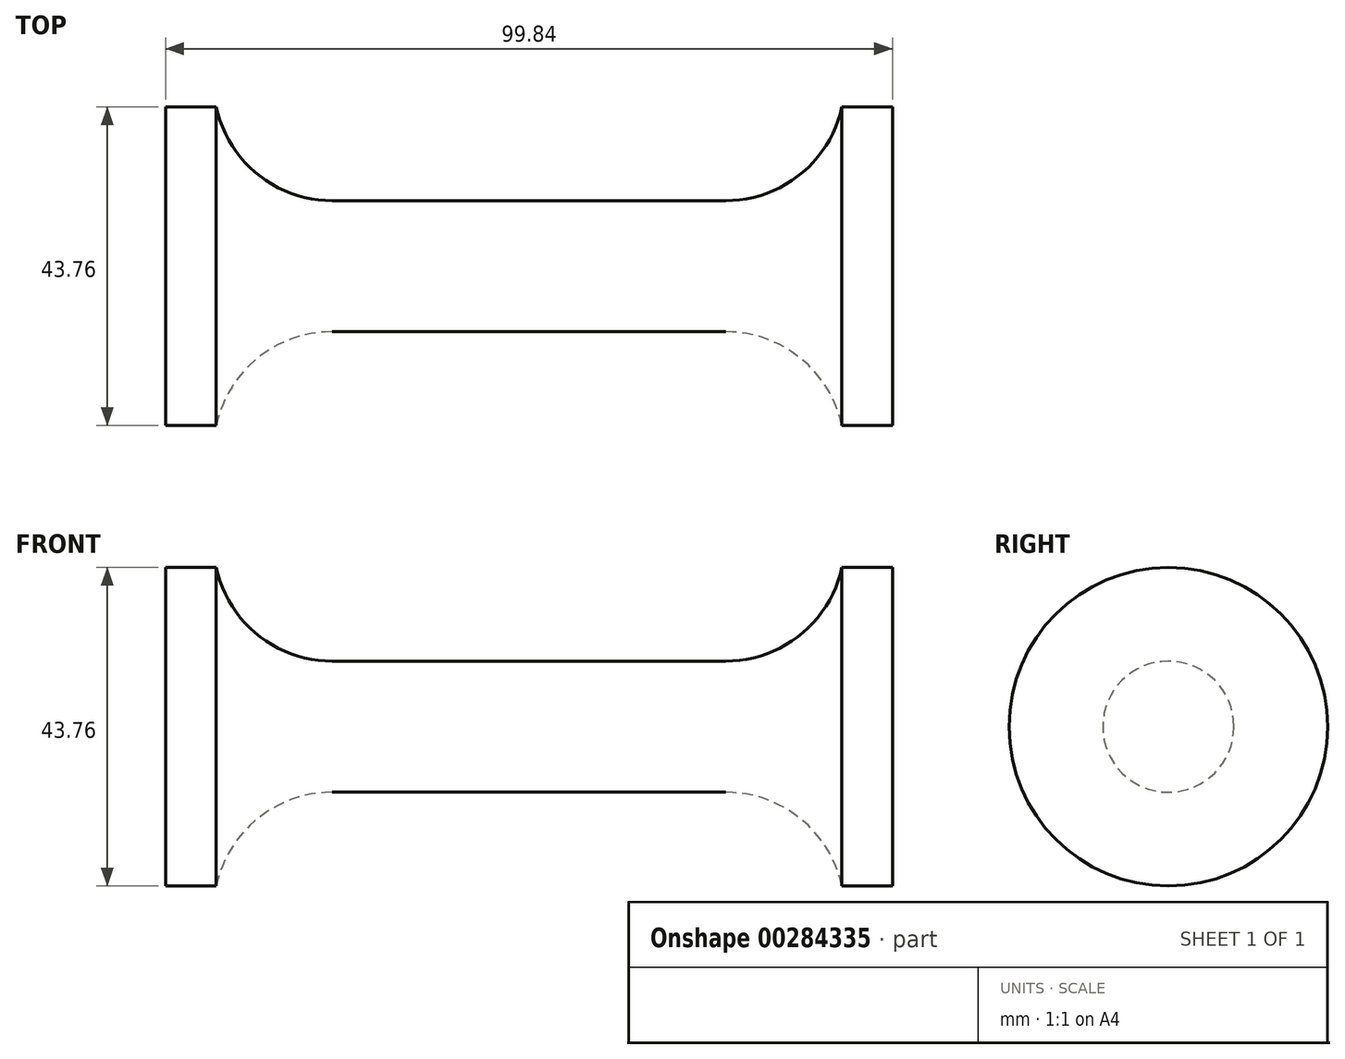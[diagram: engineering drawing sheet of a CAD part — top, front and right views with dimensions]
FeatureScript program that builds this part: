
annotation { "Feature Type Name" : "Feature", "Feature Type Description" : "" }
export const myFeature = defineFeature(function(context is Context, id is Id, definition is map)
    precondition{}
    {
        {
            var Q0;
            Q0=qCreatedBy(makeId("Front.planeOp"),FACE);
            var sketch = newSketch(context, id + "F0", { "sketchPlane" : qUnion([Q0])});
            skLineSegment(sketch, "E0", {"start": v(0, 9) * mm, "end": v(27, 9) * mm});
            skArc(sketch, "E1", {"start": v(27, 9) * mm, "mid": v(37.26, 12.62) * mm, "end": v(42.97, 21.88) * mm});
            skLineSegment(sketch, "E2", {"start": v(42.97, 21.88) * mm, "end": v(49.92, 21.88) * mm});
            skLineSegment(sketch, "E3", {"start": v(49.92, 21.88) * mm, "end": v(49.92, 0) * mm});
            skLineSegment(sketch, "E4.MirrorCS", {"start": v(0, 9) * mm, "end": v(-27, 9) * mm});
            skLineSegment(sketch, "E5.MirrorCS", {"start": v(-49.92, 21.88) * mm, "end": v(-49.92, 0) * mm});
            skLineSegment(sketch, "E6.MirrorCS", {"start": v(-42.97, 21.88) * mm, "end": v(-49.92, 21.88) * mm});
            skArc(sketch, "E7.MirrorCS", {"start": v(-27, 9) * mm, "mid": v(-37.26, 12.62) * mm, "end": v(-42.97, 21.88) * mm});
            skLineSegment(sketch, "E8", {"start": v(-49.92, 0) * mm, "end": v(49.92, 0) * mm});
            skSolve(sketch);
        }
        {
            var Q0;
            Q0 = qSketchRegion(id + "F0", true);
            var Q1;
            Q1=sQuery(id+"F0.wireOp",EDGE,"E8");
            revolve(context, id + "F1", {"entities" : qUnion([Q0]), "axis" : qUnion([Q1]), "revolveType" : RevolveType.FULL});
        }
    });
